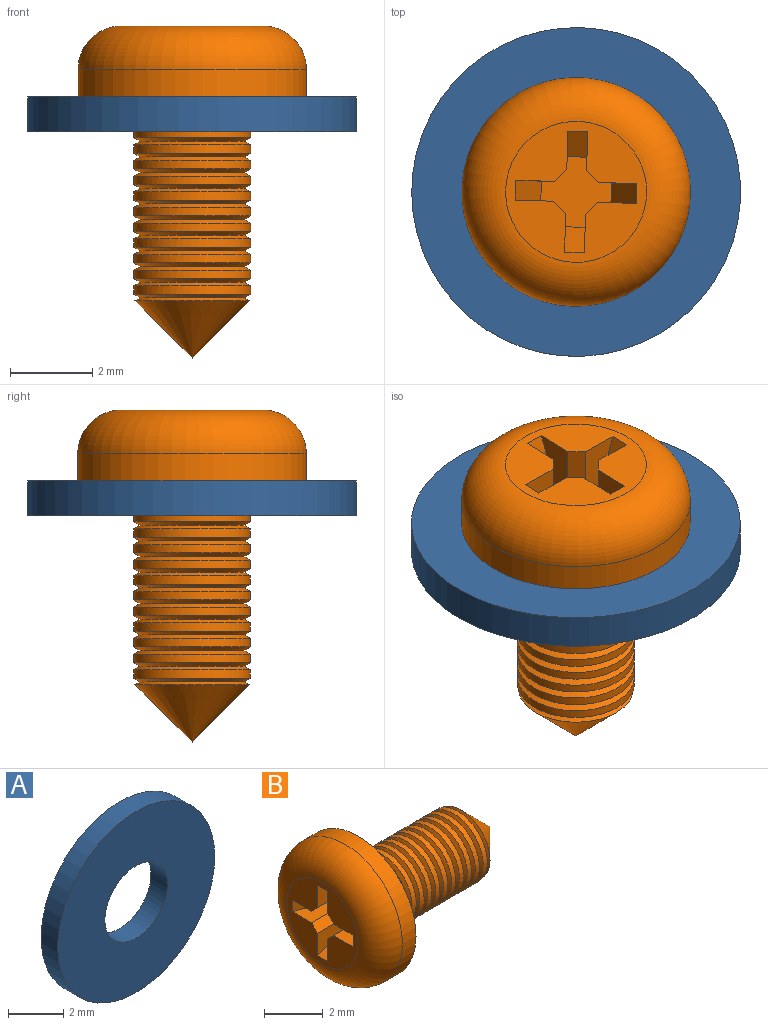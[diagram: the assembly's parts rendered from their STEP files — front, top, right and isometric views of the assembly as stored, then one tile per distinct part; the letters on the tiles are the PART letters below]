
ASSEMBLY  parts=2 mates=1
PART A: 4 faces, bbox 8x0.9x8 mm
  f0: cylinder r=1.6mm len=3.2mm, axis (0,1,0), area 8.5mm2, adj f2,f3
  f1: cylinder r=4mm len=8mm, axis (0,1,0), area 21.4mm2, adj f2,f3
  f2: plane 8x8mm, normal (0,-1,0), area 42.2mm2, adj f0,f1
  f3: plane 8x8mm, normal (0,1,0), area 42.2mm2, adj f0,f1
PART B: 61 faces, bbox 8.1x6x6 mm
  f0: cone r=1.42mm half-angle=45deg, axis (-1,0,0), area 8.6mm2, adj f1
  f1: cone r=1.26mm half-angle=60deg, axis (1,0,0), area 1.2mm2, adj f0,f2
  f2: cone r=1.5mm half-angle=60deg, axis (-1,0,0), area 1.5mm2, adj f1,f3
  f3: cylinder r=1.42mm len=2.85mm, axis (-1,0,0), area 1.8mm2, adj f2,f5
  f4: cone r=1.5mm half-angle=60deg, axis (-1,0,0), area 1.5mm2, adj f5,f6
  f5: cone r=1.26mm half-angle=60deg, axis (1,0,0), area 1.5mm2, adj f3,f4
  f6: cylinder r=1.42mm len=2.85mm, axis (-1,0,0), area 1.8mm2, adj f4,f8
  f7: cone r=1.5mm half-angle=60deg, axis (-1,0,0), area 1.5mm2, adj f8,f9
  f8: cone r=1.26mm half-angle=60deg, axis (1,0,0), area 1.5mm2, adj f6,f7
  f9: cylinder r=1.42mm len=2.85mm, axis (-1,0,0), area 1.8mm2, adj f7,f11
  f10: cone r=1.5mm half-angle=60deg, axis (-1,0,0), area 1.5mm2, adj f11,f12
  f11: cone r=1.26mm half-angle=60deg, axis (1,0,0), area 1.5mm2, adj f9,f10
  f12: cylinder r=1.42mm len=2.85mm, axis (-1,0,0), area 1.8mm2, adj f10,f14
  f13: cone r=1.5mm half-angle=60deg, axis (-1,0,0), area 1.5mm2, adj f14,f15
  f14: cone r=1.26mm half-angle=60deg, axis (1,0,0), area 1.5mm2, adj f12,f13
  f15: cylinder r=1.42mm len=2.85mm, axis (-1,0,0), area 1.8mm2, adj f13,f17
  f16: cone r=1.5mm half-angle=60deg, axis (-1,0,0), area 1.5mm2, adj f17,f18
  f17: cone r=1.26mm half-angle=60deg, axis (1,0,0), area 1.5mm2, adj f15,f16
  f18: cylinder r=1.42mm len=2.85mm, axis (-1,0,0), area 1.8mm2, adj f16,f20
  f19: cone r=1.5mm half-angle=60deg, axis (-1,0,0), area 1.5mm2, adj f20,f21
  f20: cone r=1.26mm half-angle=60deg, axis (1,0,0), area 1.5mm2, adj f18,f19
  f21: cylinder r=1.42mm len=2.85mm, axis (-1,0,0), area 1.8mm2, adj f19,f23
  f22: cone r=1.5mm half-angle=60deg, axis (-1,0,0), area 1.5mm2, adj f23,f24
  f23: cone r=1.26mm half-angle=60deg, axis (1,0,0), area 1.5mm2, adj f21,f22
  f24: cylinder r=1.42mm len=2.85mm, axis (-1,0,0), area 1.8mm2, adj f22,f26
  f25: cone r=1.5mm half-angle=60deg, axis (-1,0,0), area 1.5mm2, adj f26,f27
  f26: cone r=1.26mm half-angle=60deg, axis (1,0,0), area 1.5mm2, adj f24,f25
  f27: cylinder r=1.42mm len=2.85mm, axis (-1,0,0), area 1.8mm2, adj f25,f29
  f28: cone r=1.5mm half-angle=60deg, axis (-1,0,0), area 1.5mm2, adj f29,f35
  f29: cone r=1.26mm half-angle=60deg, axis (1,0,0), area 1.5mm2, adj f27,f28
  f30: cylinder r=1.42mm len=2.85mm, axis (-1,0,0), area 2mm2, adj f34,f60
  f31: cylinder r=2.78mm len=5.56mm, axis (-1,0,0), area 11.5mm2, adj f32,f60
  f32: torus R=1.71mm, axis (-1,0,0), area 25.2mm2, adj f31,f59
  f33: cone r=1.26mm half-angle=60deg, axis (1,0,0), area 1.5mm2, adj f34,f41
  f34: cone r=1.5mm half-angle=60deg, axis (-1,0,0), area 1.5mm2, adj f30,f33
  f35: cylinder r=1.42mm len=2.85mm, axis (-1,0,0), area 1.8mm2, adj f28,f37
  f36: cone r=1.5mm half-angle=60deg, axis (-1,0,0), area 1.5mm2, adj f37,f38
  f37: cone r=1.26mm half-angle=60deg, axis (1,0,0), area 1.5mm2, adj f35,f36
  f38: cylinder r=1.42mm len=2.85mm, axis (-1,0,0), area 1.8mm2, adj f36,f40
  f39: cone r=1.5mm half-angle=60deg, axis (-1,0,0), area 1.5mm2, adj f40,f41
  f40: cone r=1.26mm half-angle=60deg, axis (1,0,0), area 1.5mm2, adj f38,f39
  f41: cylinder r=1.42mm len=2.85mm, axis (-1,0,0), area 1.8mm2, adj f33,f39
  f42: plane 1.71x1.71mm, normal (-1,0,0), area 1.6mm2, adj f43,f44,f45,f46,f47,f48,f49,f50
  f43: plane 1.7x0.62mm, normal (-0.34,0.94,0), area 0.9mm2, adj f42,f44,f58,f59
  f44: plane 1.7x0.94mm, normal (0,0,-1), area 1.1mm2, adj f42,f43,f45,f59
  f45: plane 1.7x0.29mm, normal (0,0.71,-0.71), area 0.7mm2, adj f42,f44,f46,f59
  f46: plane 1.7x0.94mm, normal (0,1,0), area 1.1mm2, adj f42,f45,f47,f59
  f47: plane 1.7x0.62mm, normal (-0.34,0,-0.94), area 0.9mm2, adj f42,f46,f48,f59
  f48: plane 1.7x0.94mm, normal (0,-1,0), area 1.1mm2, adj f42,f47,f49,f59
  f49: plane 1.7x0.29mm, normal (0,-0.71,-0.71), area 0.7mm2, adj f42,f48,f50,f59
  f50: plane 1.7x0.94mm, normal (0,0,-1), area 1.1mm2, adj f42,f49,f51,f59
  f51: plane 1.7x0.62mm, normal (-0.34,-0.94,0), area 0.9mm2, adj f42,f50,f52,f59
  f52: plane 1.7x0.94mm, normal (0,0,1), area 1.1mm2, adj f42,f51,f53,f59
  f53: plane 1.7x0.29mm, normal (0,-0.71,0.71), area 0.7mm2, adj f42,f52,f54,f59
  f54: plane 1.7x0.94mm, normal (0,-1,0), area 1.1mm2, adj f42,f53,f55,f59
  f55: plane 1.7x0.62mm, normal (-0.34,0,0.94), area 0.9mm2, adj f42,f54,f56,f59
  f56: plane 1.7x0.94mm, normal (0,1,0), area 1.1mm2, adj f42,f55,f57,f59
  f57: plane 1.7x0.29mm, normal (0,0.71,0.71), area 0.7mm2, adj f42,f56,f58,f59
  f58: plane 1.7x0.94mm, normal (0,0,1), area 1.1mm2, adj f42,f43,f57,f59
  f59: plane 3.43x3.43mm, normal (-1,0,0), area 6.5mm2, adj f32,f43,f44,f45,f46,f47,f48,f49
  f60: plane 5.56x5.56mm, normal (1,0,0), area 17.9mm2, adj f30,f31
PLACE A rot(axis=(0.59,0.57,0.57),119.1deg) t=(52.05,3.94,0.49)mm
PLACE B rot(axis=(0.01,1,-0.01),90deg) t=(58.06,7.82,-5.42)mm
MATE fastened B.f0 <-> A.f0  axis (0,0,-1) through (57.1,7.77,-4.19)mm
